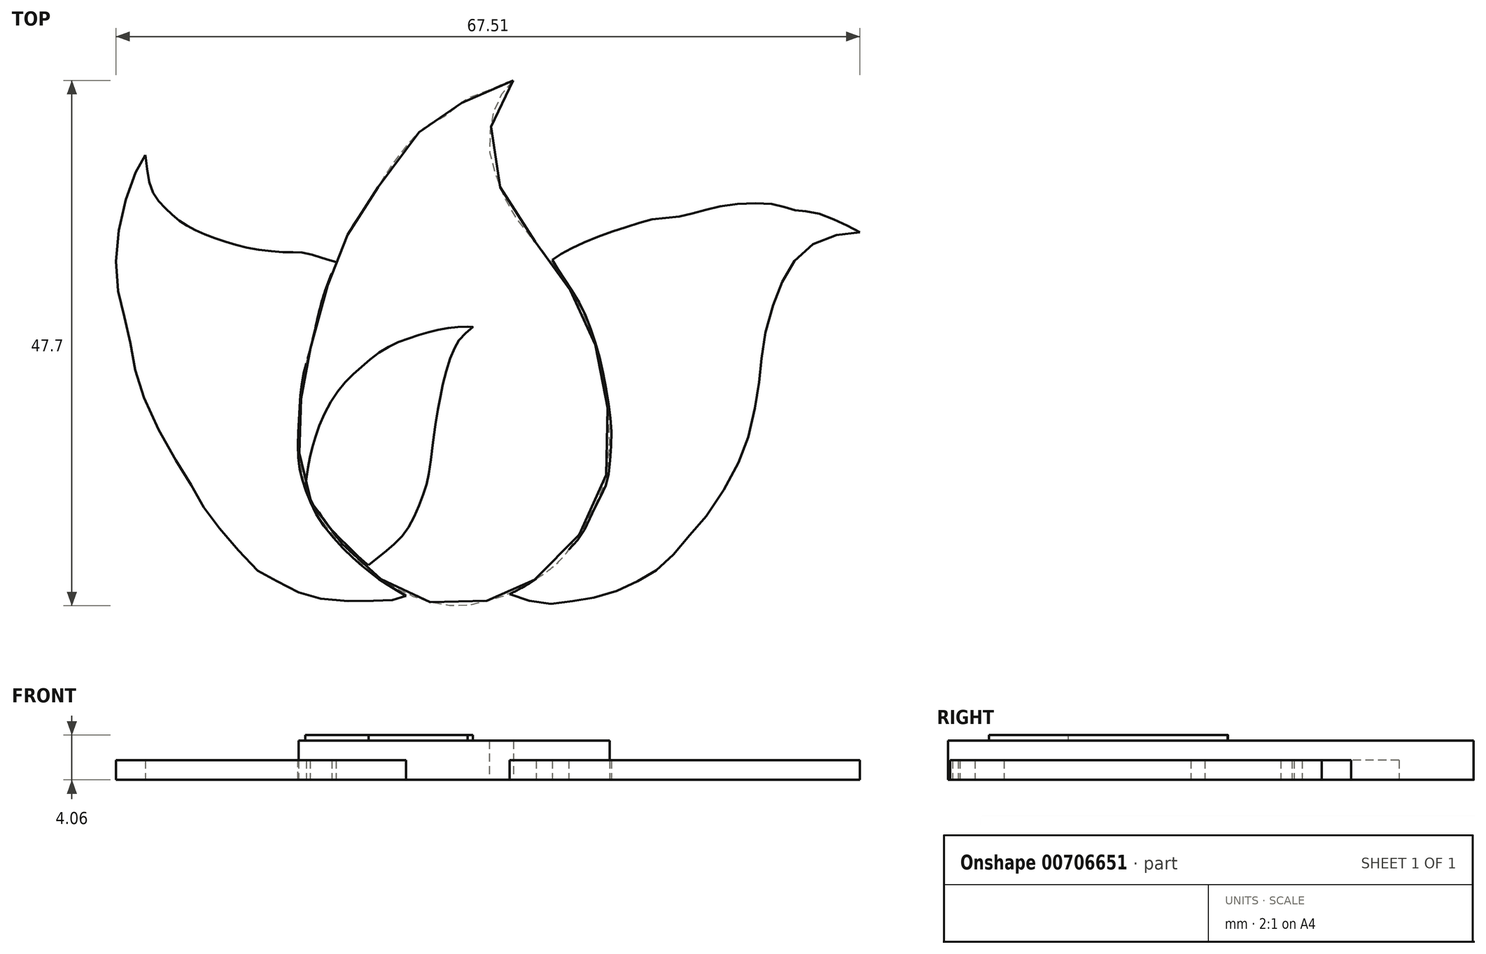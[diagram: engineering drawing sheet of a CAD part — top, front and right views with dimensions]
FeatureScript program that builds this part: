
annotation { "Feature Type Name" : "Feature", "Feature Type Description" : "" }
export const myFeature = defineFeature(function(context is Context, id is Id, definition is map)
    precondition{}
    {
        {
            var Q0;
            Q0=qCreatedBy(makeId("Top.planeOp"),FACE);
            var sketch = newSketch(context, id + "F0", { "sketchPlane" : qUnion([Q0])});
            skFitSpline(sketch, "E0", {"points": [v(-34.05, 24.01) * mm, v(-34.88, 22.6) * mm, v(-36.04, 19.12) * mm, v(-36.7, 15.05) * mm, v(-36.46, 11.23) * mm, v(-35.71, 8.4) * mm, v(-35.13, 5.25) * mm, v(-34.14, 1.85) * mm, v(-31.73, -2.96) * mm, v(-29.74, -6.2) * mm, v(-28.32, -8.6) * mm, v(-26.25, -11.1) * mm, v(-23.93, -13.67) * mm, v(-22.1, -14.67) * mm, v(-19.86, -15.83) * mm, v(-17.62, -16.33) * mm, v(-14.3, -16.5) * mm, v(-12.3, -16.41) * mm, v(-11.14, -16.33) * mm, v(-10.4, -16) * mm], "startDerivative": vector(-20.68, -30.57) * mm, "endDerivative": vector(24.83, 14) * mm});
            skFitSpline(sketch, "E1", {"points": [v(-34.05, 24.01) * mm, v(-33.39, 20.7) * mm, v(-32.14, 19.12) * mm, v(-30.81, 17.95) * mm, v(-29.15, 17.04) * mm, v(-26.91, 16.21) * mm, v(-24.42, 15.55) * mm, v(-21.43, 15.21) * mm, v(-19.6, 15.13) * mm, v(-17.62, 14.55) * mm, v(-16.7, 14.3) * mm], "startDerivative": vector(3.1, -29.18) * mm, "endDerivative": vector(12.18, -2.95) * mm});
            skFitSpline(sketch, "E2", {"points": [v(-16.7, 14.3) * mm, v(-17.62, 12.06) * mm, v(-18.28, 9.82) * mm, v(-19.2, 6) * mm, v(-19.77, 3.84) * mm, v(-20.02, 1.52) * mm, v(-20.19, -1.3) * mm, v(-20.1, -4.13) * mm, v(-19.53, -6.37) * mm, v(-18.28, -9.02) * mm, v(-15.8, -12.01) * mm, v(-13.8, -13.76) * mm, v(-12.22, -14.92) * mm, v(-10.4, -16) * mm], "startDerivative": vector(-13.32, -31.14) * mm, "endDerivative": vector(27.32, -15.35) * mm});
            skSolve(sketch);
        }
        {
            var Q0;
            Q0 = qSketchRegion(id + "F0", true);
            var Q1;
            Q1 = qSketchRegion(id + "F2", true);
            extrude(context, id + "F1", {"entities" : qUnion([Q0, Q1]), "depth" : 1.78 * mm, "offsetDistance" : 25.4 * mm});
        }
        {
            var Q0;
            Q0=qCreatedBy(makeId("Top.planeOp"),FACE);
            var sketch = newSketch(context, id + "F2", { "sketchPlane" : qUnion([Q0])});
            skFitSpline(sketch, "E3", {"points": [v(-0.67, 30.78) * mm, v(-3.14, 29.8) * mm, v(-5.09, 28.98) * mm, v(-6.73, 27.63) * mm, v(-8.3, 26.81) * mm, v(-10.17, 25.1) * mm, v(-12.42, 22.02) * mm, v(-13.84, 19.63) * mm, v(-15.11, 17.9) * mm, v(-16.16, 15.74) * mm, v(-16.68, 14.47) * mm, v(-17.73, 11.55) * mm, v(-18.48, 8.7) * mm, v(-19.3, 5.64) * mm, v(-19.75, 3.77) * mm, v(-19.9, 2.05) * mm, v(-20.12, 0) * mm, v(-20.12, -2.44) * mm, v(-19.97, -4.23) * mm, v(-19.6, -6.1) * mm, v(-18.63, -8.35) * mm, v(-17.65, -9.77) * mm, v(-16.38, -11.12) * mm, v(-14.96, -12.54) * mm, v(-13.54, -13.88) * mm, v(-11.44, -15.23) * mm, v(-9.57, -16.13) * mm, v(-7.48, -16.73) * mm, v(-5.01, -16.88) * mm, v(-2.7, -16.35) * mm, v(-0.9, -15.75) * mm, v(0.9, -14.78) * mm, v(3.3, -13.06) * mm, v(5.16, -10.67) * mm, v(6.96, -7.45) * mm, v(7.78, -4.9) * mm, v(8.08, -1.76) * mm, v(7.78, 1.9) * mm, v(7.18, 5.2) * mm, v(6.58, 7.44) * mm, v(5.61, 9.9) * mm, v(3.97, 12.52) * mm, v(2.32, 14.92) * mm, v(0.97, 16.56) * mm, v(-0.97, 19.18) * mm, v(-2.17, 22.02) * mm, v(-2.84, 24.94) * mm, v(-2.54, 27.41) * mm, v(-1.87, 29.36) * mm, v(-0.67, 30.78) * mm]});
            skSolve(sketch);
        }
        {
            var Q0;
            Q0 = qSketchRegion(id + "F2", true);
            extrude(context, id + "F3", {"entities" : qUnion([Q0]), "operationType" : NewBodyOperationType.ADD, "depth" : 3.56 * mm, "offsetDistance" : 25.4 * mm});
        }
        {
            var Q0;
            Q0=qCreatedBy(makeId("Top.planeOp"),FACE);
            var sketch = newSketch(context, id + "F4", { "sketchPlane" : qUnion([Q0])});
            skFitSpline(sketch, "E4", {"points": [v(30.78, 17.01) * mm, v(28.75, 18.03) * mm, v(26.45, 18.84) * mm, v(25.02, 18.98) * mm, v(23.74, 19.38) * mm, v(21.3, 19.65) * mm, v(17.9, 19.32) * mm, v(15.8, 18.77) * mm, v(13.85, 18.37) * mm, v(11.88, 18.16) * mm, v(10.05, 17.62) * mm, v(7.75, 16.88) * mm, v(5.58, 16) * mm, v(3.89, 15.18) * mm, v(2.87, 14.5) * mm], "startDerivative": vector(-26.01, 13.59) * mm, "endDerivative": vector(-17.12, -12.41) * mm});
            skFitSpline(sketch, "E5", {"points": [v(-0.99, -15.84) * mm, v(0.77, -16.45) * mm, v(2.94, -16.72) * mm, v(4.97, -16.45) * mm, v(7.14, -16.04) * mm, v(9.51, -15.23) * mm, v(11.47, -14.22) * mm, v(13.17, -13) * mm, v(15.06, -10.83) * mm, v(16.9, -8.73) * mm, v(19.26, -4.87) * mm, v(20.62, -1.68) * mm, v(21.43, 2.04) * mm, v(21.77, 4.62) * mm, v(22.1, 7.46) * mm, v(23.06, 10.85) * mm, v(24.14, 13.29) * mm, v(25.77, 15.39) * mm, v(28.27, 16.67) * mm, v(30.78, 17.01) * mm], "startDerivative": vector(38.83, -15.3) * mm, "endDerivative": vector(49.08, 3.22) * mm});
            skFitSpline(sketch, "E6", {"points": [v(2.87, 14.5) * mm, v(3.82, 12.95) * mm, v(5.24, 10.78) * mm, v(6.4, 8.14) * mm, v(7.27, 5.16) * mm, v(7.95, 1.57) * mm, v(8.22, -1) * mm, v(8.09, -3.99) * mm, v(7.68, -6.09) * mm, v(6.73, -7.98) * mm, v(5.85, -9.88) * mm, v(4.5, -11.7) * mm, v(2.87, -13.13) * mm, v(1.38, -14.49) * mm, v(-0.99, -15.84) * mm], "startDerivative": vector(14.3, -24.7) * mm, "endDerivative": vector(-34.26, -17.18) * mm});
            skSolve(sketch);
        }
        {
            var Q0;
            Q0 = qSketchRegion(id + "F4", true);
            extrude(context, id + "F5", {"entities" : qUnion([Q0]), "operationType" : NewBodyOperationType.ADD, "depth" : 1.78 * mm, "offsetDistance" : 25.4 * mm});
        }
        {
            var Q0;
            Q0=makeQuery(id+"F3.opExtrude","CAP_FACE",FACE,{"disambiguationData":[OSD([sQuery(id+"F2.wireOp",EDGE,"E3")])],"isStart":false});
            var sketch = newSketch(context, id + "F6", { "sketchPlane" : qUnion([Q0])});
            skFitSpline(sketch, "E7", {"points": [v(-8.6, 20.19) * mm, v(-8.45, 17.64) * mm, v(-8.07, 15.68) * mm, v(-7.45, 14.13) * mm, v(-7, 13.32) * mm, v(-6.24, 12.4) * mm, v(-6.22, 12.4) * mm], "startDerivative": vector(0.4, -10.7) * mm, "endDerivative": vector(0.62, 0.35) * mm});
            skSolve(sketch);
        }
        {
            var Q0;
            Q0=makeQuery(id+"F6.imprint","IMPRINT",FACE,{"disambiguationData":[TD([[makeQuery(id+"F6.imprint","IMPRINT",EDGE,{"derivedFrom":makeQuery(id+"F3.opExtrude","CAP_EDGE",EDGE,{"disambiguationData":[OSD([sQuery(id+"F2.wireOp",EDGE,"E3")])],"isStart":false})}),1.0]])]});
            var sketch = newSketch(context, id + "F7", { "sketchPlane" : qUnion([Q0])});
            skFitSpline(sketch, "E8", {"points": [v(-6.18, -4.95) * mm, v(-3.5, -4.72) * mm, v(-1.1, -4.6) * mm, v(1, -4.89) * mm, v(2.02, -5.17) * mm, v(3, -6.03) * mm, v(3.68, -7.45) * mm, v(4.25, -9.1) * mm, v(4.02, -11.21) * mm, v(3.45, -12.7) * mm, v(2.14, -13.94) * mm, v(0.49, -14.85) * mm, v(-0.65, -15.14) * mm], "startDerivative": vector(26.4, 2.16) * mm, "endDerivative": vector(-16.05, -2.89) * mm});
            skSolve(sketch);
        }
        {
            var Q0;
            Q0=sQuery(id+"F7.wireOp",EDGE,"E8");
            extrude(context, id + "F8", {"bodyType" : ToolBodyType.SURFACE, "surfaceEntities" : qUnion([Q0]), "depth" : 0.4 * mm, "offsetDistance" : 25.4 * mm});
        }
        {
            var Q0;
            Q0=makeQuery(id+"F6.imprint","IMPRINT",FACE,{"disambiguationData":[TD([[makeQuery(id+"F6.imprint","IMPRINT",EDGE,{"derivedFrom":makeQuery(id+"F3.opExtrude","CAP_EDGE",EDGE,{"disambiguationData":[OSD([sQuery(id+"F2.wireOp",EDGE,"E3")])],"isStart":false})}),1.0]])]});
            var sketch = newSketch(context, id + "F9", { "sketchPlane" : qUnion([Q0])});
            skFitSpline(sketch, "E9", {"points": [v(-4.8, 8.45) * mm, v(-7.17, 8.23) * mm, v(-9.57, 7.58) * mm, v(-12.17, 6.5) * mm, v(-14.58, 4.67) * mm, v(-16.75, 2.34) * mm, v(-18.51, -1.21) * mm, v(-19.2, -3.89) * mm, v(-19.54, -6.02) * mm], "startDerivative": vector(-20.74, -1.18) * mm, "endDerivative": vector(-2.85, -19.27) * mm});
            skFitSpline(sketch, "E10", {"points": [v(-19.54, -6.02) * mm, v(-19.08, -7.29) * mm, v(-18.17, -8.62) * mm, v(-17.25, -9.88) * mm, v(-16, -11.18) * mm, v(-14.35, -12.79) * mm, v(-13.81, -13.2) * mm], "startDerivative": vector(2.3, -8.08) * mm, "endDerivative": vector(4.12, -2.93) * mm});
            skFitSpline(sketch, "E11", {"points": [v(-13.81, -13.2) * mm, v(-12.74, -12.37) * mm, v(-11.18, -11.03) * mm, v(-10.1, -9.65) * mm, v(-9.23, -7.82) * mm, v(-8.58, -6.02) * mm, v(-8.23, -4.23) * mm, v(-7.66, 0) * mm, v(-7.2, 2.46) * mm, v(-6.6, 4.98) * mm, v(-5.87, 6.74) * mm, v(-5.25, 7.61) * mm, v(-4.34, 8.45) * mm, v(-4.8, 8.45) * mm], "startDerivative": vector(15.07, 11.8) * mm, "endDerivative": vector(-17.53, -2.71) * mm});
            skSolve(sketch);
        }
        {
            var Q0;
            Q0 = qSketchRegion(id + "F9", true);
            extrude(context, id + "F10", {"entities" : qUnion([Q0]), "operationType" : NewBodyOperationType.ADD, "depth" : 0.5 * mm, "offsetDistance" : 25.4 * mm});
        }
        {
            var Q0;
            Q0=makeQuery(id+"F6.imprint","IMPRINT",FACE,{"disambiguationData":[TD([[makeQuery(id+"F6.imprint","IMPRINT",EDGE,{"derivedFrom":makeQuery(id+"F3.opExtrude","CAP_EDGE",EDGE,{"disambiguationData":[OSD([sQuery(id+"F2.wireOp",EDGE,"E3")])],"isStart":false})}),1.0]])]});
            var sketch = newSketch(context, id + "F11", { "sketchPlane" : qUnion([Q0])});
            skFitSpline(sketch, "E12", {"points": [v(-4.34, 8.45) * mm, v(-2.7, 8.27) * mm, v(-0.3, 7.6) * mm, v(1.84, 6.36) * mm, v(3.22, 4.8) * mm], "startDerivative": vector(7.18, -0.5) * mm, "endDerivative": vector(5.1, -6.69) * mm});
            skSolve(sketch);
        }
        {
            var Q0;
            Q0=sQuery(id+"F11.wireOp",EDGE,"E12");
            extrude(context, id + "F12", {"bodyType" : ToolBodyType.SURFACE, "surfaceEntities" : qUnion([Q0]), "depth" : 0.4 * mm, "offsetDistance" : 25.4 * mm});
        }
        {
            var Q0;
            Q0=makeQuery(id+"F10.opExtrude","CAP_FACE",FACE,{"disambiguationData":[OSD([sQuery(id+"F9.wireOp",EDGE,"E9"),sQuery(id+"F9.wireOp",EDGE,"E10"),sQuery(id+"F9.wireOp",EDGE,"E11")])],"isStart":false});
            var sketch = newSketch(context, id + "F13", { "sketchPlane" : qUnion([Q0])});
            skFitSpline(sketch, "E13", {"points": [v(-15.55, -7.36) * mm, v(-14.46, -6.84) * mm, v(-13.75, -6) * mm, v(-12.89, -1.96) * mm, v(-12.39, 0.53) * mm, v(-11.84, 2.35) * mm, v(-11.38, 3.13) * mm, v(-11.03, 3.6) * mm, v(-10.38, 3.99) * mm, v(-9.92, 4.09) * mm], "startDerivative": vector(11.08, 4.75) * mm, "endDerivative": vector(6.58, 1) * mm});
            skSolve(sketch);
        }
        {
            var Q0;
            Q0=sQuery(id+"F13.wireOp",EDGE,"E13");
            extrude(context, id + "F14", {"bodyType" : ToolBodyType.SURFACE, "surfaceEntities" : qUnion([Q0]), "depth" : -0.5 * mm, "offsetDistance" : 25.4 * mm});
        }
        {
            var Q0;
            Q0=qCreatedBy(makeId("Top.planeOp"),FACE);
            var sketch = newSketch(context, id + "F15", { "sketchPlane" : qUnion([Q0])});
            skFitSpline(sketch, "E14", {"points": [v(-2.15, -16.18) * mm, v(-3.28, -17.5) * mm, v(-4.46, -19.54) * mm, v(-5.1, -22.53) * mm, v(-5.14, -25.2) * mm, v(-5.05, -28.39) * mm, v(-5.82, -31.02) * mm, v(-7, -32.6) * mm, v(-8.27, -34.1) * mm, v(-10.27, -35.42) * mm, v(-12.22, -36.37) * mm, v(-13.85, -36.69) * mm], "startDerivative": vector(-14.5, -15.82) * mm, "endDerivative": vector(-21.1, -2.6) * mm});
            skSolve(sketch);
        }
        {
            var Q0;
            Q0=sQuery(id+"F15.wireOp",EDGE,"E14");
            extrude(context, id + "F16", {"bodyType" : ToolBodyType.SURFACE, "surfaceEntities" : qUnion([Q0]), "depth" : 1 * mm, "offsetDistance" : 25.4 * mm});
        }
        {
            var Q0;
            Q0=qCreatedBy(makeId("Top.planeOp"),FACE);
            var sketch = newSketch(context, id + "F17", { "sketchPlane" : qUnion([Q0])});
            skCircle(sketch, "E15", {"center": v(-21.52, -36.56) * mm, "radius": 7.4 * mm});
            skSolve(sketch);
        }
        {
            var Q0;
            Q0=sQuery(id+"F17.wireOp",EDGE,"E15");
            extrude(context, id + "F18", {"bodyType" : ToolBodyType.SURFACE, "surfaceEntities" : qUnion([Q0]), "depth" : 1.5 * mm, "offsetDistance" : 25.4 * mm});
        }
    });
